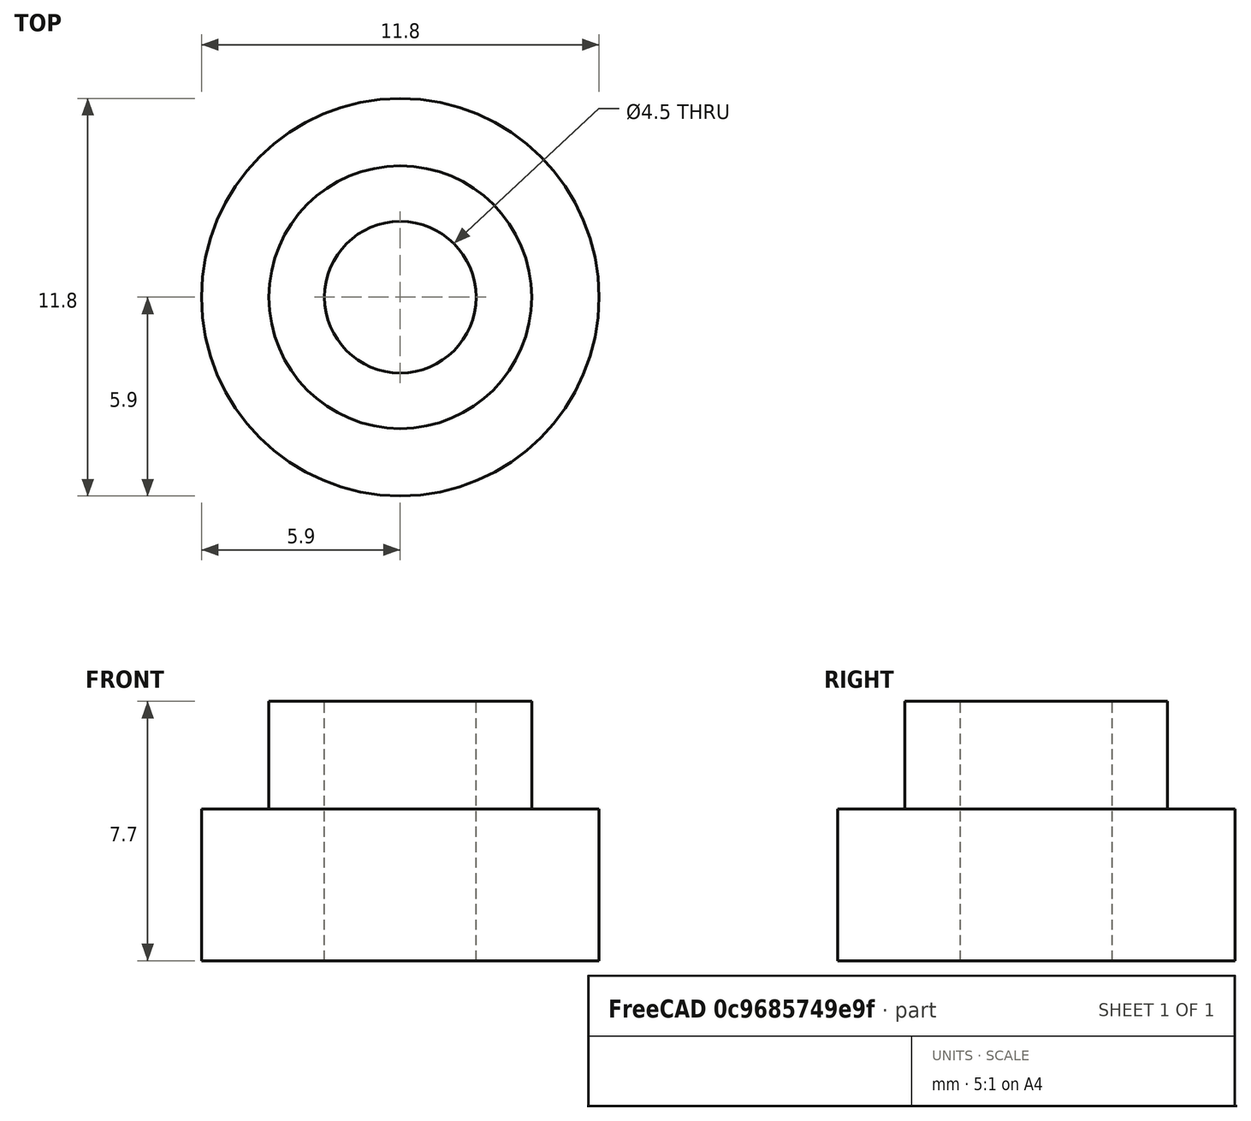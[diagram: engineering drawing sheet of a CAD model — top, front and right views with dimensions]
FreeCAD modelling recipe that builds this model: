
FCSTD DOCUMENT  (FreeCAD 0.20R29177 +426 (Git))
Label: CablePulleyBearingHub
License: All rights reserved
LicenseURL: http://en.wikipedia.org/wiki/All_rights_reserved
objects: App::DocumentObjectGroup×3, PartDesign::CoordinateSystem×1, App::FeaturePython×1, Sketcher::SketchObject×1, PartDesign::Revolution×1, PartDesign::Body×1, App::Part×1
note: 5 computed .brp shape members not serialized (recipe doc carries the construction recipe); baked Part::Feature solids carry a one-line shape summary decoded from their .brp

FEATURE [App::DocumentObjectGroup] Parts
FEATURE [PartDesign::CoordinateSystem] LCS_Origin
  AttacherType = Attacher::AttachEngine3D
  MapMode = 2
  Support = -> [X_Axis]
FEATURE [App::FeaturePython] Variables  # WARN: FeaturePython — macro-defined, semantics opaque (R4)
  Type = App::PropertyContainer
FEATURE [App::DocumentObjectGroup] Constraints
FEATURE [App::DocumentObjectGroup] Configurations
FEATURE [Sketcher::SketchObject] Sketch
  FullyConstrained = true
  MapMode = 5
  Placement = pos=(0,0,0) rot=(1,0,0;1.5708rad)
  Support = -> [XZ_Plane001]
  sketch-geometry (6):
    g0: LineSegment StartX=2.25 StartY=-4.5 StartZ=0 EndX=2.25 EndY=3.2 EndZ=0
    g1: LineSegment StartX=2.25 StartY=3.2 StartZ=0 EndX=3.9 EndY=3.2 EndZ=0
    g2: LineSegment StartX=3.9 StartY=3.2 StartZ=0 EndX=3.9 EndY=0 EndZ=0
    g3: LineSegment StartX=3.9 StartY=0 StartZ=0 EndX=5.9 EndY=0 EndZ=0
    g4: LineSegment StartX=5.9 StartY=0 StartZ=0 EndX=5.9 EndY=-4.5 EndZ=0
    g5: LineSegment StartX=5.9 StartY=-4.5 StartZ=0 EndX=2.25 EndY=-4.5 EndZ=0
  constraints (18):
    c: Vertical(g0)
    c: Coincident(g0,g1)
    c: Horizontal(g1)
    c: Coincident(g1,g2)
    c: Vertical(g2)
    c: Coincident(g2,g3)
    c: Horizontal(g3)
    c: Coincident(g3,g4)
    c: Vertical(g4)
    c: Coincident(g4,g5)
    c: Coincident(g5,g0)
    c: Horizontal(g5)
    c: DistanceX(g-1,g0) = 2.25
    c: DistanceX(g-1,g1) = 3.9
    c: DistanceX(g3,g3) = 2
    c: DistanceY(g4,g4) = 4.5
    c: DistanceY(g2,g2) = 3.2
    c: PointOnObject(g2,g-1)
FEATURE [PartDesign::Revolution] Revolution
  Angle = 360
  Axis = (0,-2e-16,1)
  Base = (0,0,0)
  Placement = pos=(0,0,0) rot=(1,0,0;1.5708rad)
  Profile = -> Sketch
  ReferenceAxis = -> Sketch [V_Axis]
  Reversed = true
FEATURE [PartDesign::Body] Body
  Group = -> [Sketch,Revolution]
  Origin = -> Origin001
  Tip = -> Revolution
FEATURE [App::Part] Assembly
  AssemblyType = Part::Link
  Group = -> [LCS_Origin,Variables,Constraints,Configurations,Body]
  Origin = -> Origin
  Type = Assembly
